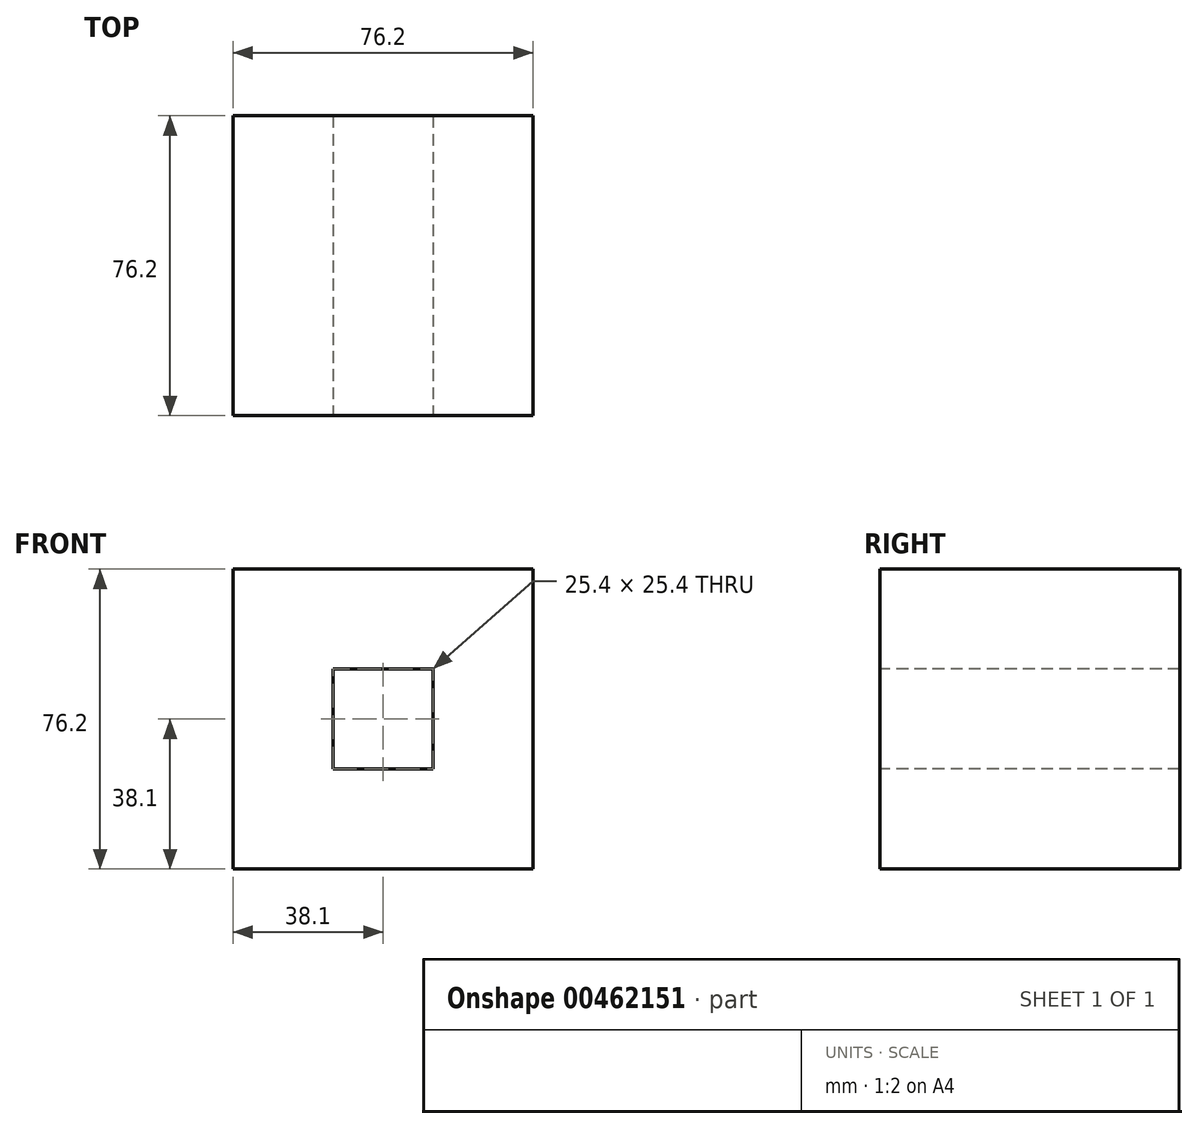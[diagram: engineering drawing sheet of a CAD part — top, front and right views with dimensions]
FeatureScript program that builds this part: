
annotation { "Feature Type Name" : "Feature", "Feature Type Description" : "" }
export const myFeature = defineFeature(function(context is Context, id is Id, definition is map)
    precondition{}
    {
        {
            var Q0;
            Q0=qCreatedBy(makeId("Front.planeOp"),FACE);
            var sketch = newSketch(context, id + "F0", { "sketchPlane" : qUnion([Q0])});
            skLineSegment(sketch, "E0.bottom", {"start": v(-38.1, 38.1) * mm, "end": v(38.1, 38.1) * mm});
            skLineSegment(sketch, "E0.top", {"start": v(-38.1, -38.1) * mm, "end": v(38.1, -38.1) * mm});
            skLineSegment(sketch, "E0.left", {"start": v(-38.1, 38.1) * mm, "end": v(-38.1, -38.1) * mm});
            skLineSegment(sketch, "E0.right", {"start": v(38.1, 38.1) * mm, "end": v(38.1, -38.1) * mm});
            skPoint(sketch, "E0.middle", {"position": v(0, 0) * mm});
            skSolve(sketch);
        }
        {
            var Q0;
            Q0=makeQuery(id+"F0.imprint","IMPRINT",FACE,{"disambiguationData":[TD([[makeQuery(id+"F0.imprint","IMPRINT",EDGE,{"derivedFrom":sQuery(id+"F0.wireOp",EDGE,"E0.bottom")}),-1.0]])]});
            extrude(context, id + "F1", {"entities" : qUnion([Q0]), "depth" : 76.2 * mm});
        }
        {
            var Q0;
            Q0=makeQuery(id+"F1.opExtrude","CAP_FACE",FACE,{"disambiguationData":[OSD([sQuery(id+"F0.wireOp",EDGE,"E0.bottom"),sQuery(id+"F0.wireOp",EDGE,"E0.top"),sQuery(id+"F0.wireOp",EDGE,"E0.left"),sQuery(id+"F0.wireOp",EDGE,"E0.right")])],"isStart":false});
            var sketch = newSketch(context, id + "F2", { "sketchPlane" : qUnion([Q0])});
            skLineSegment(sketch, "E1.bottom", {"start": v(-12.7, 12.7) * mm, "end": v(12.7, 12.7) * mm});
            skLineSegment(sketch, "E1.top", {"start": v(-12.7, -12.7) * mm, "end": v(12.7, -12.7) * mm});
            skLineSegment(sketch, "E1.left", {"start": v(-12.7, 12.7) * mm, "end": v(-12.7, -12.7) * mm});
            skLineSegment(sketch, "E1.right", {"start": v(12.7, 12.7) * mm, "end": v(12.7, -12.7) * mm});
            skPoint(sketch, "E1.middle", {"position": v(0, 0) * mm});
            skSolve(sketch);
        }
        {
            var Q0;
            Q0 = qSketchRegion(id + "F2", true);
            var Q1;
            Q1=makeQuery(id+"F2.imprint","IMPRINT",FACE,{"disambiguationData":[TD([[makeQuery(id+"F2.imprint","IMPRINT",EDGE,{"derivedFrom":sQuery(id+"F2.wireOp",EDGE,"E1.bottom")}),-1.0]])]});
            extrude(context, id + "F3", {"entities" : qUnion([Q0, Q1]), "operationType" : NewBodyOperationType.REMOVE, "oppositeDirection" : true, "depth" : 76.2 * mm});
        }
    });
